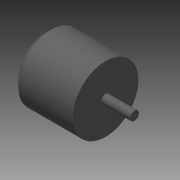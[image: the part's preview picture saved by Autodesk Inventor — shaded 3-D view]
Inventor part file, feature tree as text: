
AUTODESK INVENTOR PART (.ipt)
format: ipt  version: 2014 SP1 (Build 180222100, 222)  size: 90,112 bytes
history: native  units: in
note: dims shown in document units (in); Inventor stores cm internally (conversion verified against a paired STEP export)
features: other x3, sketch x1
ambient origin geometry x8: Origin, YZ Plane, XZ Plane, XY Plane, X Axis, Y Axis, Z Axis, Center Point
bodies: Solid1 (feature_tree)
feature tree (4):
  other  "6354motor.ipt"
  other  "Solid1::6354motor.ipt"
  other  "TaggingFeature1"
  sketch  "Sketch1"  dims[d0=0.3937in d1=2.126in d2=0.1575in d3=1.0236in d5=0.2in]
